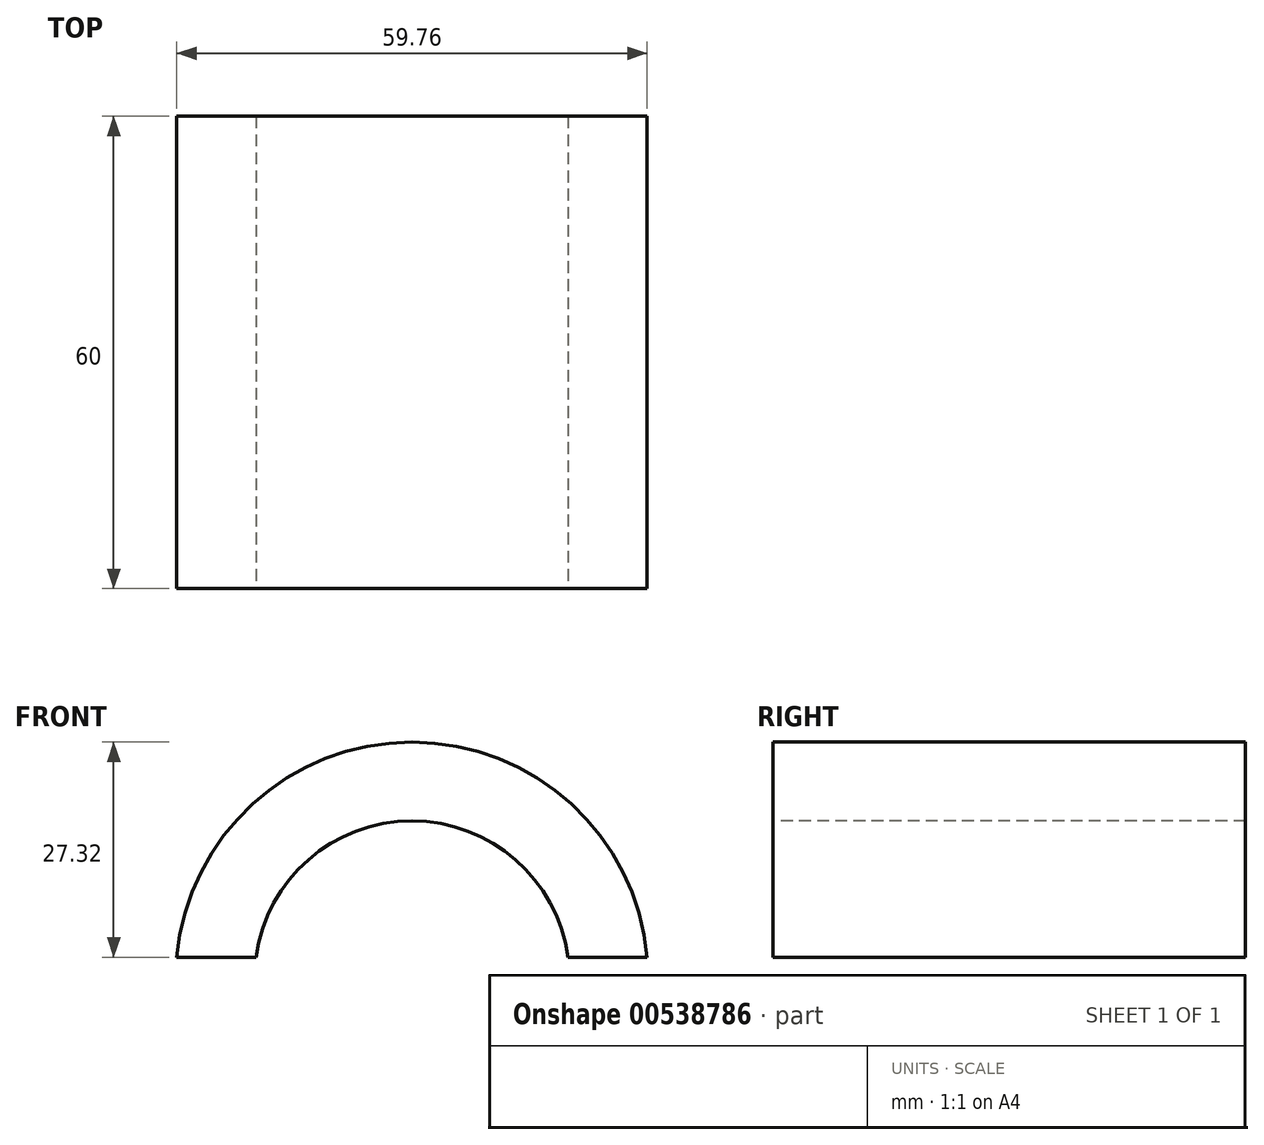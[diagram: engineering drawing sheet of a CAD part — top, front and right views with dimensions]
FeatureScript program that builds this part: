
annotation { "Feature Type Name" : "Feature", "Feature Type Description" : "" }
export const myFeature = defineFeature(function(context is Context, id is Id, definition is map)
    precondition{}
    {
        {
            var Q0;
            Q0=qCreatedBy(makeId("Front.planeOp"),FACE);
            var sketch = newSketch(context, id + "F0", { "sketchPlane" : qUnion([Q0])});
            skArc(sketch, "E0", {"start": v(19.82, 0) * mm, "mid": v(0, 17.32) * mm, "end": v(-19.82, 0) * mm});
            skArc(sketch, "E1", {"start": v(29.88, 0) * mm, "mid": v(0, 27.32) * mm, "end": v(-29.88, 0) * mm});
            skLineSegment(sketch, "E2", {"start": v(-19.82, 0) * mm, "end": v(-29.88, 0) * mm});
            skLineSegment(sketch, "E3", {"start": v(19.82, 0) * mm, "end": v(29.88, 0) * mm});
            skLineSegment(sketch, "E4", {"start": v(0, 33.8) * mm, "end": v(0, -8.22) * mm, "construction": true});
            skPoint(sketch, "E4.endSnap0", {"position": v(0, 17.32) * mm});
            skSolve(sketch);
        }
        {
            var Q0;
            Q0=makeQuery(id+"F0.imprint","IMPRINT",FACE,{"disambiguationData":[TD([[makeQuery(id+"F0.imprint","IMPRINT",EDGE,{"derivedFrom":sQuery(id+"F0.wireOp",EDGE,"E0")}),-1.0]])]});
            extrude(context, id + "F1", {"entities" : qUnion([Q0]), "oppositeDirection" : true, "depth" : 60 * mm, "offsetDistance" : 25 * mm});
        }
    });
